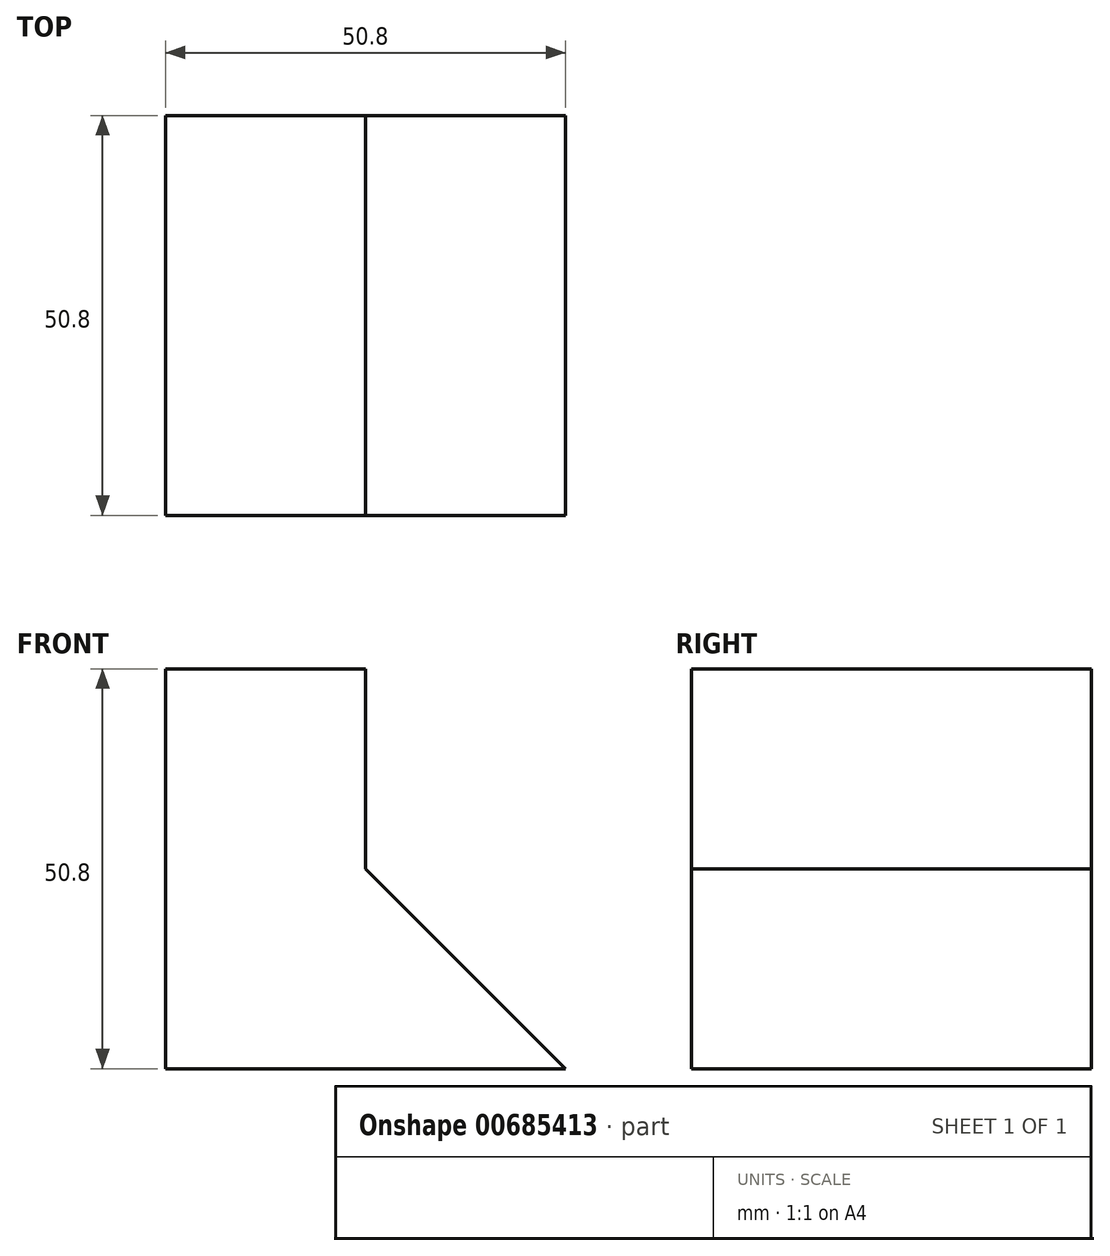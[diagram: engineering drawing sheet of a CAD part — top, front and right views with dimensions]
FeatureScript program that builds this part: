
annotation { "Feature Type Name" : "Feature", "Feature Type Description" : "" }
export const myFeature = defineFeature(function(context is Context, id is Id, definition is map)
    precondition{}
    {
        {
            var Q0;
            Q0=qCreatedBy(makeId("Front.planeOp"),FACE);
            var sketch = newSketch(context, id + "F0", { "sketchPlane" : qUnion([Q0])});
            skLineSegment(sketch, "E0", {"start": v(0, 0) * mm, "end": v(0, 50.8) * mm});
            skLineSegment(sketch, "E1", {"start": v(0, 50.8) * mm, "end": v(25.4, 50.8) * mm});
            skLineSegment(sketch, "E2", {"start": v(25.4, 50.8) * mm, "end": v(25.4, 25.4) * mm});
            skLineSegment(sketch, "E3", {"start": v(25.4, 25.4) * mm, "end": v(50.8, 0) * mm});
            skLineSegment(sketch, "E4", {"start": v(50.8, 0) * mm, "end": v(0, 0) * mm});
            skSolve(sketch);
        }
        {
            var Q0;
            Q0=makeQuery(id+"F0.imprint","IMPRINT",FACE,{"disambiguationData":[TD([[makeQuery(id+"F0.imprint","IMPRINT",EDGE,{"derivedFrom":sQuery(id+"F0.wireOp",EDGE,"E0")}),-1.0]])]});
            extrude(context, id + "F1", {"entities" : qUnion([Q0]), "depth" : 50.8 * mm, "offsetDistance" : 25.4 * mm});
        }
    });
